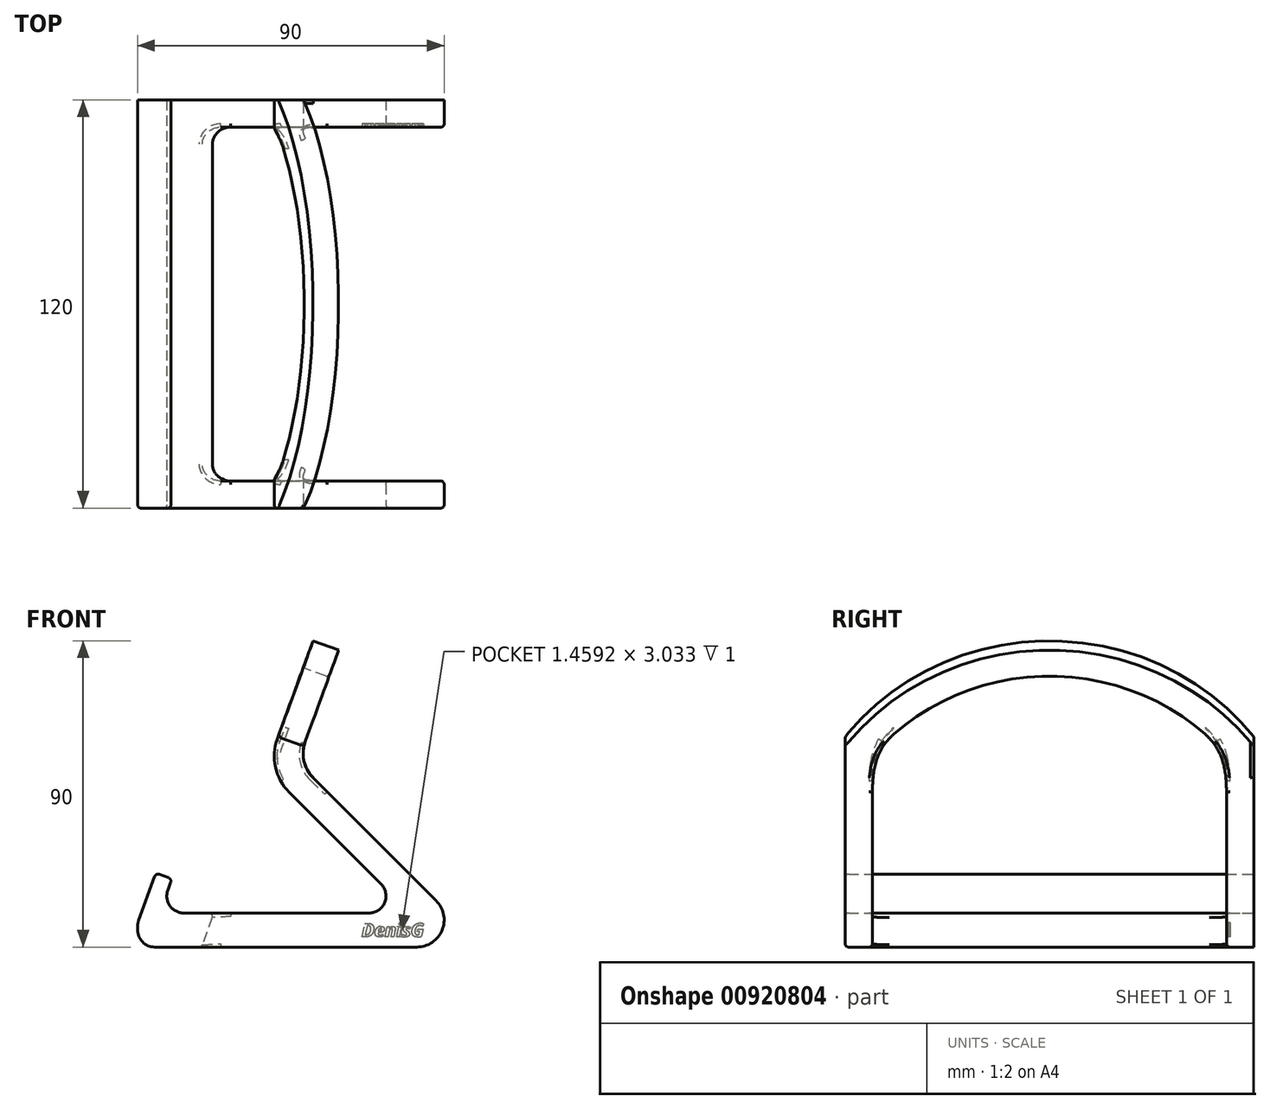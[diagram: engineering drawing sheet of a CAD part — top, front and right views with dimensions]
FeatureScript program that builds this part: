
annotation { "Feature Type Name" : "Feature", "Feature Type Description" : "" }
export const myFeature = defineFeature(function(context is Context, id is Id, definition is map)
    precondition{}
    {
        {
            var Q0;
            Q0=qCreatedBy(makeId("Front.planeOp"),FACE);
            var sketch = newSketch(context, id + "F0", { "sketchPlane" : qUnion([Q0])});
            skLineSegment(sketch, "E0", {"start": v(0, 0) * mm, "end": v(90, 0) * mm});
            skLineSegment(sketch, "E1", {"start": v(90, 0) * mm, "end": v(90, 11.31) * mm});
            skLineSegment(sketch, "E2", {"start": v(90, 11.31) * mm, "end": v(47.01, 54.3) * mm});
            skLineSegment(sketch, "E3", {"start": v(47.01, 54.3) * mm, "end": v(59.01, 87.26) * mm});
            skLineSegment(sketch, "E4", {"start": v(59.01, 87.26) * mm, "end": v(51.5, 90) * mm});
            skLineSegment(sketch, "E5", {"start": v(51.5, 90) * mm, "end": v(37.75, 52.25) * mm});
            skLineSegment(sketch, "E6", {"start": v(37.75, 52.25) * mm, "end": v(80, 10) * mm});
            skLineSegment(sketch, "E7", {"start": v(80, 10) * mm, "end": v(6.41, 10) * mm});
            skLineSegment(sketch, "E8", {"start": v(6.41, 10) * mm, "end": v(10.05, 20) * mm});
            skLineSegment(sketch, "E9", {"start": v(0, 7) * mm, "end": v(0, 0) * mm});
            skLineSegment(sketch, "E10", {"start": v(37.75, 52.25) * mm, "end": v(22.61, 10.65) * mm, "construction": true});
            skLineSegment(sketch, "E11", {"start": v(0, 7) * mm, "end": v(5.35, 21.71) * mm});
            skLineSegment(sketch, "E12", {"start": v(5.35, 21.71) * mm, "end": v(10.05, 20) * mm});
            skSolve(sketch);
        }
        {
            var Q0;
            Q0=qSketchRegion(id+"F0",true);
            extrude(context, id + "F1", {"entities" : qUnion([Q0]), "depth" : 120 * mm, "offsetDistance" : 25 * mm});
        }
        {
            var Q0;
            Q0=makeQuery(id+"F1.opExtrude","SWEPT_EDGE",EDGE,{"disambiguationData":[OSD([sQuery(id+"F0.wireOp",EDGE,"E6"),sQuery(id+"F0.wireOp",EDGE,"E7")])]});
            var Q1;
            Q1=makeQuery(id+"F1.opExtrude","SWEPT_EDGE",EDGE,{"disambiguationData":[OSD([sQuery(id+"F0.wireOp",EDGE,"E0"),sQuery(id+"F0.wireOp",EDGE,"E9")])]});
            var Q2;
            Q2=makeQuery(id+"F1.opExtrude","SWEPT_EDGE",EDGE,{"disambiguationData":[OSD([sQuery(id+"F0.wireOp",EDGE,"E9"),sQuery(id+"F0.wireOp",EDGE,"E11")])]});
            var Q3;
            Q3=makeQuery(id+"F1.opExtrude","SWEPT_EDGE",EDGE,{"disambiguationData":[OSD([sQuery(id+"F0.wireOp",EDGE,"E7"),sQuery(id+"F0.wireOp",EDGE,"E8")])]});
            fillet(context, id + "F2", {"entities" : qUnion([Q0, Q1, Q2, Q3]), "radius" : 5 * mm, "tangentPropagation" : true, "allowEdgeOverflow" : false});
        }
        {
            var Q0;
            Q0=makeQuery(id+"F1.opExtrude","SWEPT_FACE",FACE,{"disambiguationData":[OSD([sQuery(id+"F0.wireOp",EDGE,"E5")])]});
            var sketch = newSketch(context, id + "F3", { "sketchPlane" : qUnion([Q0])});
            skArc(sketch, "E13", {"start": v(120, 72.18) * mm, "mid": v(60, 102.18) * mm, "end": v(0, 72.18) * mm});
            skLineSegment(sketch, "E14.top", {"start": v(8, 6.4) * mm, "end": v(112, 6.4) * mm});
            skLineSegment(sketch, "E14.left", {"start": v(8, 68.76) * mm, "end": v(8, 6.4) * mm});
            skLineSegment(sketch, "E14.right", {"start": v(112, 68.76) * mm, "end": v(112, 6.4) * mm});
            skArc(sketch, "E15", {"start": v(112, 68.76) * mm, "mid": v(60, 93.76) * mm, "end": v(8, 68.76) * mm});
            skSolve(sketch);
        }
        {
            var Q0;
            {var subQ0=sQuery(id+"F3.wireOp",EDGE,"E13");var subQ1=sQuery(id+"F0.wireOp",EDGE,"E5");var subQ2=makeQuery(id+"F1.opExtrude","CAP_EDGE",EDGE,{"disambiguationData":[OSD([subQ1])],"isStart":true});var subQ3=makeQuery(id+"F3.imprint","INTERSECT",VERTEX,{"derivedFrom":[subQ2,subQ0]});Q0=makeQuery(id+"F3.imprint","IMPRINT",FACE,{"disambiguationData":[TD([[makeQuery(id+"F3.imprint","IMPRINT",EDGE,{"disambiguationData":[TD([[subQ3,1.0]])],"derivedFrom":subQ0}),-1.0]])]});}
            var Q1;
            {var subQ0=sQuery(id+"F3.wireOp",EDGE,"E13");var subQ1=sQuery(id+"F0.wireOp",EDGE,"E5");var subQ2=makeQuery(id+"F1.opExtrude","CAP_EDGE",EDGE,{"disambiguationData":[OSD([subQ1])],"isStart":false});var subQ3=makeQuery(id+"F3.imprint","INTERSECT",VERTEX,{"derivedFrom":[subQ2,subQ0]});Q1=makeQuery(id+"F3.imprint","IMPRINT",FACE,{"disambiguationData":[TD([[makeQuery(id+"F3.imprint","IMPRINT",EDGE,{"disambiguationData":[TD([[subQ3,-1.0]])],"derivedFrom":subQ0}),-1.0]])]});}
            var Q2;
            Q2=makeQuery(id+"F3.imprint","IMPRINT",FACE,{"disambiguationData":[TD([[makeQuery(id+"F3.imprint","IMPRINT",EDGE,{"derivedFrom":sQuery(id+"F3.wireOp",EDGE,"E14.bottom")}),1.0]])]});
            var Q3;
            {var subQ0=sQuery(id+"F3.wireOp",EDGE,"E14.top");Q3=makeQuery(id+"F3.imprint","IMPRINT",FACE,{"disambiguationData":[TD([[makeQuery(id+"F3.imprint","IMPRINT",EDGE,{"derivedFrom":subQ0}),1.0]])]});}
            var Q4;
            {var subQ0=sQuery(id+"F3.wireOp",EDGE,"E14.bottom");Q4=makeQuery(id+"F3.imprint","IMPRINT",FACE,{"disambiguationData":[TD([[makeQuery(id+"F3.imprint","IMPRINT",EDGE,{"derivedFrom":subQ0}),-1.0]])]});}
            var Q5;
            {var subQ0=sQuery(id+"F3.wireOp",EDGE,"E15");Q5=makeQuery(id+"F3.imprint","IMPRINT",FACE,{"disambiguationData":[TD([[makeQuery(id+"F3.imprint","IMPRINT",EDGE,{"derivedFrom":subQ0}),1.0]])]});}
            extrude(context, id + "F4", {"entities" : qUnion([Q0, Q1, Q2, Q3, Q4, Q5]), "operationType" : NewBodyOperationType.REMOVE, "endBound" : BoundingType.THROUGH_ALL, "oppositeDirection" : true, "depth" : 25 * mm, "offsetDistance" : 25 * mm});
        }
        {
            var Q0;
            Q0=makeQuery(id+"F4.boolean.opBoolean","COPY",EDGE,{"derivedFrom":makeQuery(id+"F4.opExtrude","SWEPT_EDGE",EDGE,{"disambiguationData":[OSD([sQuery(id+"F3.wireOp",EDGE,"E14.bottom"),sQuery(id+"F3.wireOp",EDGE,"E14.left"),sQuery(id+"F3.wireOp",EDGE,"E15")])]})});
            var Q1;
            Q1=makeQuery(id+"F4.boolean.opBoolean","COPY",EDGE,{"derivedFrom":makeQuery(id+"F4.opExtrude","SWEPT_EDGE",EDGE,{"disambiguationData":[OSD([sQuery(id+"F3.wireOp",EDGE,"E14.bottom"),sQuery(id+"F3.wireOp",EDGE,"E14.right"),sQuery(id+"F3.wireOp",EDGE,"E15")])]})});
            var Q2;
            {var subQ0=sQuery(id+"F3.wireOp",EDGE,"E13");var subQ1=sQuery(id+"F0.wireOp",EDGE,"E5");Q2=makeQuery(id+"F4.boolean.opBoolean","COPY",EDGE,{"derivedFrom":makeQuery(id+"F4.opExtrude","SWEPT_EDGE",EDGE,{"disambiguationData":[OSD([subQ1,subQ0]),TDD([makeQuery(id+"F3.imprint","INTERSECT",VERTEX,{"derivedFrom":[makeQuery(id+"F1.opExtrude","CAP_EDGE",EDGE,{"disambiguationData":[OSD([subQ1])],"isStart":false}),subQ0]})])]})});}
            var Q3;
            {var subQ0=sQuery(id+"F3.wireOp",EDGE,"E13");var subQ1=sQuery(id+"F0.wireOp",EDGE,"E5");Q3=makeQuery(id+"F4.boolean.opBoolean","COPY",EDGE,{"derivedFrom":makeQuery(id+"F4.opExtrude","SWEPT_EDGE",EDGE,{"disambiguationData":[OSD([subQ1,subQ0]),TDD([makeQuery(id+"F3.imprint","INTERSECT",VERTEX,{"derivedFrom":[makeQuery(id+"F1.opExtrude","CAP_EDGE",EDGE,{"disambiguationData":[OSD([subQ1])],"isStart":true}),subQ0]})])]})});}
            fillet(context, id + "F5", {"entities" : qUnion([Q0, Q1, Q2, Q3]), "radius" : 20 * mm, "tangentPropagation" : true, "allowEdgeOverflow" : false});
        }
        {
            var Q0;
            {var subQ0=sQuery(id+"F0.wireOp",EDGE,"E2");var subQ1=sQuery(id+"F0.wireOp",EDGE,"E1");Q0=makeQuery(id+"F4.boolean.opBoolean","SPLIT",EDGE,{"disambiguationData":[TD([makeQuery(id+"F4.opExtrude","SWEPT_FACE",FACE,{"disambiguationData":[OSD([sQuery(id+"F3.wireOp",EDGE,"E14.right")])]})])],"derivedFrom":makeQuery(id+"F1.opExtrude","SWEPT_EDGE",EDGE,{"disambiguationData":[OSD([subQ1,subQ0])]})});}
            var Q1;
            {var subQ0=sQuery(id+"F0.wireOp",EDGE,"E0");var subQ1=sQuery(id+"F0.wireOp",EDGE,"E1");Q1=makeQuery(id+"F4.boolean.opBoolean","SPLIT",EDGE,{"disambiguationData":[TD([makeQuery(id+"F4.opExtrude","SWEPT_FACE",FACE,{"disambiguationData":[OSD([sQuery(id+"F3.wireOp",EDGE,"E14.right")])]})])],"derivedFrom":makeQuery(id+"F1.opExtrude","SWEPT_EDGE",EDGE,{"disambiguationData":[OSD([subQ0,subQ1])]})});}
            var Q2;
            {var subQ0=sQuery(id+"F0.wireOp",EDGE,"E0");var subQ1=sQuery(id+"F0.wireOp",EDGE,"E1");Q2=makeQuery(id+"F4.boolean.opBoolean","SPLIT",EDGE,{"disambiguationData":[TD([makeQuery(id+"F4.opExtrude","SWEPT_FACE",FACE,{"disambiguationData":[OSD([sQuery(id+"F3.wireOp",EDGE,"E14.left")])]})])],"derivedFrom":makeQuery(id+"F1.opExtrude","SWEPT_EDGE",EDGE,{"disambiguationData":[OSD([subQ0,subQ1])]})});}
            var Q3;
            {var subQ0=sQuery(id+"F0.wireOp",EDGE,"E2");var subQ1=sQuery(id+"F0.wireOp",EDGE,"E1");Q3=makeQuery(id+"F4.boolean.opBoolean","SPLIT",EDGE,{"disambiguationData":[TD([makeQuery(id+"F4.opExtrude","SWEPT_FACE",FACE,{"disambiguationData":[OSD([sQuery(id+"F3.wireOp",EDGE,"E14.left")])]})])],"derivedFrom":makeQuery(id+"F1.opExtrude","SWEPT_EDGE",EDGE,{"disambiguationData":[OSD([subQ1,subQ0])]})});}
            fillet(context, id + "F6", {"entities" : qUnion([Q0, Q1, Q2, Q3]), "radius" : 8 * mm, "tangentPropagation" : true, "allowEdgeOverflow" : false});
        }
        {
            var Q0;
            {var subQ0=sQuery(id+"F0.wireOp",EDGE,"E3");var subQ1=sQuery(id+"F0.wireOp",EDGE,"E2");Q0=makeQuery(id+"F4.boolean.opBoolean","SPLIT",EDGE,{"disambiguationData":[TD([makeQuery(id+"F4.opExtrude","SWEPT_FACE",FACE,{"disambiguationData":[OSD([sQuery(id+"F3.wireOp",EDGE,"E14.right")])]})])],"derivedFrom":makeQuery(id+"F1.opExtrude","SWEPT_EDGE",EDGE,{"disambiguationData":[OSD([subQ1,subQ0])]})});}
            var Q1;
            {var subQ0=sQuery(id+"F0.wireOp",EDGE,"E3");var subQ1=sQuery(id+"F0.wireOp",EDGE,"E2");Q1=makeQuery(id+"F4.boolean.opBoolean","SPLIT",EDGE,{"disambiguationData":[TD([makeQuery(id+"F4.opExtrude","SWEPT_FACE",FACE,{"disambiguationData":[OSD([sQuery(id+"F3.wireOp",EDGE,"E14.left")])]})])],"derivedFrom":makeQuery(id+"F1.opExtrude","SWEPT_EDGE",EDGE,{"disambiguationData":[OSD([subQ1,subQ0])]})});}
            fillet(context, id + "F7", {"entities" : qUnion([Q0, Q1]), "radius" : 10 * mm, "tangentPropagation" : true, "allowEdgeOverflow" : false});
        }
        {
            var Q0;
            {var subQ0=sQuery(id+"F0.wireOp",EDGE,"E6");var subQ1=sQuery(id+"F0.wireOp",EDGE,"E5");Q0=makeQuery(id+"F4.boolean.opBoolean","SPLIT",EDGE,{"disambiguationData":[TD([makeQuery(id+"F4.opExtrude","SWEPT_FACE",FACE,{"disambiguationData":[OSD([sQuery(id+"F3.wireOp",EDGE,"E14.left")])]})])],"derivedFrom":makeQuery(id+"F1.opExtrude","SWEPT_EDGE",EDGE,{"disambiguationData":[OSD([subQ1,subQ0])]})});}
            var Q1;
            {var subQ0=sQuery(id+"F0.wireOp",EDGE,"E6");var subQ1=sQuery(id+"F0.wireOp",EDGE,"E5");Q1=makeQuery(id+"F4.boolean.opBoolean","SPLIT",EDGE,{"disambiguationData":[TD([makeQuery(id+"F4.opExtrude","SWEPT_FACE",FACE,{"disambiguationData":[OSD([sQuery(id+"F3.wireOp",EDGE,"E14.right")])]})])],"derivedFrom":makeQuery(id+"F1.opExtrude","SWEPT_EDGE",EDGE,{"disambiguationData":[OSD([subQ1,subQ0])]})});}
            fillet(context, id + "F8", {"entities" : qUnion([Q0, Q1]), "radius" : 15 * mm, "tangentPropagation" : true, "allowEdgeOverflow" : false});
        }
        {
            var Q0;
            Q0=makeQuery(id+"F1.opExtrude","SWEPT_EDGE",EDGE,{"disambiguationData":[OSD([sQuery(id+"F0.wireOp",EDGE,"E11"),sQuery(id+"F0.wireOp",EDGE,"E12")])]});
            var Q1;
            Q1=makeQuery(id+"F1.opExtrude","SWEPT_EDGE",EDGE,{"disambiguationData":[OSD([sQuery(id+"F0.wireOp",EDGE,"E8"),sQuery(id+"F0.wireOp",EDGE,"E12")])]});
            fillet(context, id + "F9", {"entities" : qUnion([Q0, Q1]), "radius" : 1 * mm, "tangentPropagation" : true, "allowEdgeOverflow" : false});
        }
        {
            var Q0;
            {var subQ0=sQuery(id+"F3.wireOp",EDGE,"E14.right");Q0=makeQuery(id+"F4.boolean.opBoolean","COPY",EDGE,{"disambiguationData":[topologyDisambiguationEdgeConnected([makeQuery(id+"F4.opExtrude","CAP_FACE",FACE,{"disambiguationData":[OSD([sQuery(id+"F3.wireOp",EDGE,"E14.top"),sQuery(id+"F3.wireOp",EDGE,"E14.left"),subQ0,sQuery(id+"F3.wireOp",EDGE,"E15")])],"isStart":true})])],"derivedFrom":makeQuery(id+"F4.opExtrude","CAP_EDGE",EDGE,{"disambiguationData":[OSD([subQ0])],"isStart":true})});}
            var Q1;
            {var subQ0=sQuery(id+"F3.wireOp",EDGE,"E14.left");Q1=makeQuery(id+"F4.boolean.opBoolean","COPY",EDGE,{"disambiguationData":[topologyDisambiguationEdgeConnected([makeQuery(id+"F4.opExtrude","CAP_FACE",FACE,{"disambiguationData":[OSD([sQuery(id+"F3.wireOp",EDGE,"E14.top"),subQ0,sQuery(id+"F3.wireOp",EDGE,"E14.right"),sQuery(id+"F3.wireOp",EDGE,"E15")])],"isStart":true})])],"derivedFrom":makeQuery(id+"F4.opExtrude","CAP_EDGE",EDGE,{"disambiguationData":[OSD([subQ0])],"isStart":true})});}
            fillet(context, id + "F10", {"entities" : qUnion([Q0, Q1]), "radius" : 5 * mm, "tangentPropagation" : true, "allowEdgeOverflow" : false});
        }
        {
            var Q0;
            Q0=makeQuery(id+"F1.opExtrude","CAP_EDGE",EDGE,{"disambiguationData":[OSD([sQuery(id+"F0.wireOp",EDGE,"E7")])],"isStart":false});
            var Q1;
            Q1=makeQuery(id+"F4.boolean.opBoolean","INTERSECT",EDGE,{"derivedFrom":[makeQuery(id+"F1.opExtrude","SWEPT_FACE",FACE,{"disambiguationData":[OSD([sQuery(id+"F0.wireOp",EDGE,"E7")])]}),makeQuery(id+"F4.opExtrude","SWEPT_FACE",FACE,{"disambiguationData":[OSD([sQuery(id+"F3.wireOp",EDGE,"E14.left")])]})]});
            var Q2;
            Q2=makeQuery(id+"F4.boolean.opBoolean","INTERSECT",EDGE,{"derivedFrom":[makeQuery(id+"F1.opExtrude","SWEPT_FACE",FACE,{"disambiguationData":[OSD([sQuery(id+"F0.wireOp",EDGE,"E2")])]}),makeQuery(id+"F4.opExtrude","SWEPT_FACE",FACE,{"disambiguationData":[OSD([sQuery(id+"F3.wireOp",EDGE,"E14.left")])]})]});
            fillet(context, id + "F11", {"entities" : qUnion([Q0, Q1, Q2]), "radius" : 1 * mm, "tangentPropagation" : true, "allowEdgeOverflow" : false});
        }
        {
            var Q0;
            Q0=makeQuery(id+"F4.boolean.opBoolean","COPY",FACE,{"derivedFrom":makeQuery(id+"F4.opExtrude","SWEPT_FACE",FACE,{"disambiguationData":[OSD([sQuery(id+"F3.wireOp",EDGE,"E14.left")])]})});
            var sketch = newSketch(context, id + "F12", { "sketchPlane" : qUnion([Q0])});
            skText(sketch, "E16", { "text": "DenisG", "fontName": "OpenSans-BoldItalic.ttf"});
            const initialGuessF12  = {"E16": [0.06573, 0.003, 1, 0, 0.004]};
            skSetInitialGuess(sketch, initialGuessF12);
            skSolve(sketch);
        }
        {
            var Q0;
            Q0 = qSketchRegion(id + "F12", true);
            extrude(context, id + "F13", {"entities" : qUnion([Q0]), "operationType" : NewBodyOperationType.REMOVE, "oppositeDirection" : true, "depth" : 1 * mm, "offsetDistance" : 25 * mm});
        }
    });
